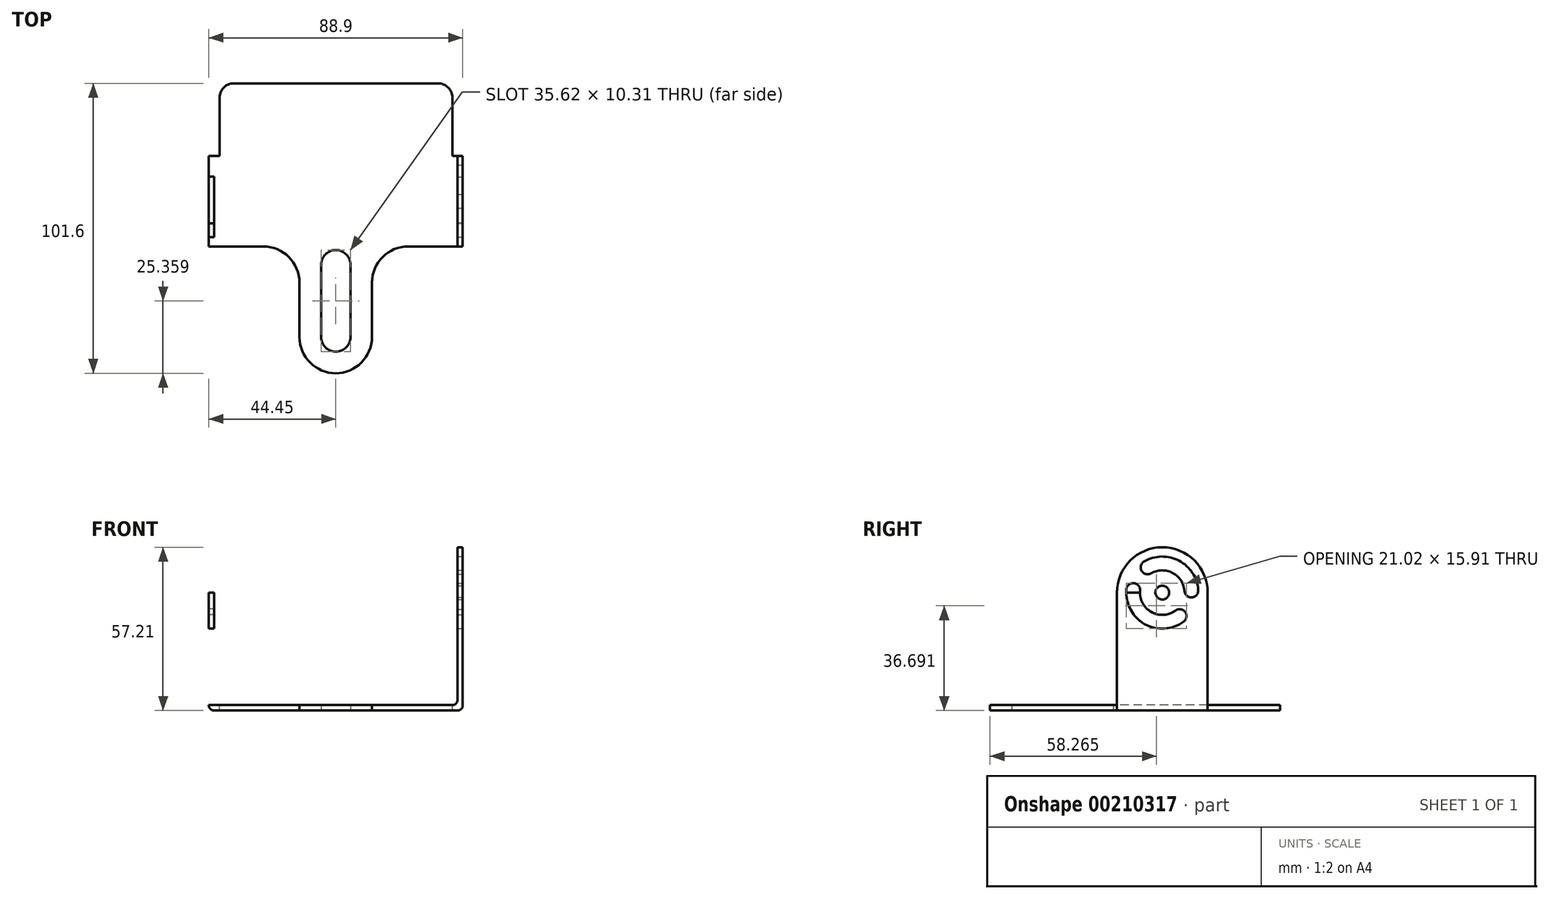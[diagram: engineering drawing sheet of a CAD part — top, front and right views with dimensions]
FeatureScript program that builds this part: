
annotation { "Feature Type Name" : "Feature", "Feature Type Description" : "" }
export const myFeature = defineFeature(function(context is Context, id is Id, definition is map)
    precondition{}
    {
        {
            var Q0;
            Q0=qCreatedBy(makeId("Top.planeOp"),FACE);
            var sketch = newSketch(context, id + "F0", { "sketchPlane" : qUnion([Q0])});
            skLineSegment(sketch, "E0.bottom", {"start": v(44.45, 15.88) * mm, "end": v(-44.45, 15.88) * mm});
            skLineSegment(sketch, "E0.top", {"start": v(44.45, -15.88) * mm, "end": v(25.4, -15.88) * mm});
            skLineSegment(sketch, "E0.left", {"start": v(44.45, 15.88) * mm, "end": v(44.45, -15.88) * mm});
            skLineSegment(sketch, "E0.right", {"start": v(-44.45, 15.88) * mm, "end": v(-44.45, -15.88) * mm});
            skPoint(sketch, "E0.middle", {"position": v(0, 0) * mm});
            skArc(sketch, "E1.0.endCap", {"start": v(12.7, -47.62) * mm, "mid": v(0, -60.33) * mm, "end": v(-12.7, -47.62) * mm});
            skLineSegment(sketch, "E1.0.left", {"start": v(12.7, -28.58) * mm, "end": v(12.7, -47.62) * mm});
            skLineSegment(sketch, "E1.0.right", {"start": v(-12.7, -28.57) * mm, "end": v(-12.7, -47.62) * mm});
            skArc(sketch, "E2.0.endCap", {"start": v(5.16, -47.62) * mm, "mid": v(0, -52.78) * mm, "end": v(-5.16, -47.62) * mm});
            skLineSegment(sketch, "E2.0.left", {"start": v(5.16, -22.32) * mm, "end": v(5.16, -47.62) * mm});
            skLineSegment(sketch, "E2.0.right", {"start": v(-5.16, -22.32) * mm, "end": v(-5.16, -47.62) * mm});
            skArc(sketch, "E3", {"start": v(5.16, -22.32) * mm, "mid": v(0, -17.16) * mm, "end": v(-5.16, -22.32) * mm});
            skLineSegment(sketch, "E4.trimOffspring", {"start": v(-25.4, -15.88) * mm, "end": v(-44.45, -15.88) * mm});
            skPoint(sketch, "E1.0.startCap.center.orphan", {"position": v(0, -15.88) * mm});
            skPoint(sketch, "E5.visualSharp", {"position": v(-12.7, -15.87) * mm});
            skArc(sketch, "E5.filletArc", {"start": v(-12.7, -28.57) * mm, "mid": v(-16.42, -19.6) * mm, "end": v(-25.4, -15.87) * mm});
            skPoint(sketch, "E6.visualSharp", {"position": v(12.7, -15.88) * mm});
            skArc(sketch, "E6.filletArc", {"start": v(25.4, -15.87) * mm, "mid": v(16.42, -19.6) * mm, "end": v(12.7, -28.57) * mm});
            skSolve(sketch);
        }
        {
            var Q0;
            Q0 = qSketchRegion(id + "F0", true);
            extrude(context, id + "F1", {"entities" : qUnion([Q0]), "depth" : 1.9 * mm, "offsetDistance" : 25.4 * mm});
        }
        {
            var Q0;
            Q0=makeQuery(id+"F1.opExtrude","SWEPT_FACE",FACE,{"disambiguationData":[OSD([sQuery(id+"F0.wireOp",EDGE,"E0.right")])]});
            var sketch = newSketch(context, id + "F2", { "sketchPlane" : qUnion([Q0])});
            skLineSegment(sketch, "E7", {"start": v(-15.87, 0) * mm, "end": v(-15.87, 41.27) * mm});
            skLineSegment(sketch, "E8", {"start": v(-15.88, 41.28) * mm, "end": v(15.88, 41.28) * mm});
            skLineSegment(sketch, "E9", {"start": v(15.87, 41.28) * mm, "end": v(15.88, 0) * mm});
            skArc(sketch, "E10", {"start": v(-15.88, 41.28) * mm, "mid": v(0, 57.15) * mm, "end": v(15.87, 41.28) * mm});
            skCircle(sketch, "E11", {"center": v(0, 41.28) * mm, "radius": 2.41 * mm});
            skArc(sketch, "E12", {"start": v(-10.1, 42.39) * mm, "mid": v(-4.48, 50.4) * mm, "end": v(5.3, 49.94) * mm});
            skArc(sketch, "E13", {"start": v(10.1, 42.39) * mm, "mid": v(5, 32.44) * mm, "end": v(-6.14, 33.18) * mm});
            skArc(sketch, "E14.0.startCap", {"start": v(-7.7, 42.12) * mm, "mid": v(-10.36, 39.99) * mm, "end": v(-12.5, 42.65) * mm});
            skArc(sketch, "E14.0.endCap", {"start": v(6.56, 52) * mm, "mid": v(7.36, 48.68) * mm, "end": v(4.04, 47.88) * mm});
            skArc(sketch, "E14.0.left", {"start": v(-12.5, 42.65) * mm, "mid": v(-5.54, 52.56) * mm, "end": v(6.56, 52) * mm});
            skArc(sketch, "E14.0.right", {"start": v(-7.7, 42.12) * mm, "mid": v(-3.41, 48.23) * mm, "end": v(4.04, 47.88) * mm});
            skArc(sketch, "E15.0.startCap", {"start": v(7.7, 42.12) * mm, "mid": v(9.84, 44.79) * mm, "end": v(12.5, 42.65) * mm});
            skArc(sketch, "E15.0.endCap", {"start": v(-7.6, 31.26) * mm, "mid": v(-8.07, 34.64) * mm, "end": v(-4.68, 35.1) * mm});
            skArc(sketch, "E15.0.left", {"start": v(12.5, 42.65) * mm, "mid": v(6.2, 30.34) * mm, "end": v(-7.6, 31.26) * mm});
            skArc(sketch, "E15.0.right", {"start": v(7.7, 42.12) * mm, "mid": v(3.82, 34.53) * mm, "end": v(-4.68, 35.1) * mm});
            skSolve(sketch);
        }
        {
            var Q0;
            {var subQ13=sQuery(id+"F2.wireOp",EDGE,"E15.0.endCap");Q0=makeQuery(id+"F2.imprint","IMPRINT",FACE,{"disambiguationData":[TD([[makeQuery(id+"F2.imprint","IMPRINT",EDGE,{"derivedFrom":subQ13}),1.0]])]});}
            var Q1;
            {var subQ1=sQuery(id+"F2.wireOp",EDGE,"E10");Q1=makeQuery(id+"F2.imprint","IMPRINT",FACE,{"disambiguationData":[TD([[makeQuery(id+"F2.imprint","IMPRINT",EDGE,{"derivedFrom":subQ1}),-1.0]])]});}
            extrude(context, id + "F3", {"entities" : qUnion([Q0, Q1]), "operationType" : NewBodyOperationType.ADD, "oppositeDirection" : true, "depth" : 1.9 * mm, "offsetDistance" : 25.4 * mm});
        }
        {
            var Q0;
            Q0=makeQuery(id+"F1.opExtrude","CAP_EDGE",EDGE,{"disambiguationData":[OSD([sQuery(id+"F0.wireOp",EDGE,"E0.right")])],"isStart":true});
            var Q1;
            Q1=makeQuery(id+"F3.opExtrude","CAP_EDGE",EDGE,{"disambiguationData":[OSD([sQuery(id+"F0.wireOp",EDGE,"E0.right")])],"isStart":false});
            fillet(context, id + "F4", {"entities" : qUnion([Q0, Q1]), "radius" : 1.84 * mm, "tangentPropagation" : true, "allowEdgeOverflow" : false});
        }
        {
            var Q0;
            Q0=makeQuery(id+"F1.opExtrude","SWEPT_FACE",FACE,{"disambiguationData":[OSD([sQuery(id+"F0.wireOp",EDGE,"E0.left")])]});
            var sketch = newSketch(context, id + "F5", { "sketchPlane" : qUnion([Q0])});
            skCircle(sketch, "E16", {"center": v(0, 41.34) * mm, "radius": 2.41 * mm});
            skArc(sketch, "E17", {"start": v(6.06, 33.12) * mm, "mid": v(-5, 32.44) * mm, "end": v(-10.17, 42.24) * mm});
            skArc(sketch, "E18", {"start": v(10.18, 42.07) * mm, "mid": v(4.77, 50.37) * mm, "end": v(-5.14, 50.16) * mm});
            skArc(sketch, "E19.0.startCap", {"start": v(4.63, 35.06) * mm, "mid": v(8, 34.55) * mm, "end": v(7.49, 31.18) * mm});
            skArc(sketch, "E19.0.endCap", {"start": v(-12.57, 42.45) * mm, "mid": v(-9.96, 44.64) * mm, "end": v(-7.77, 42.03) * mm});
            skArc(sketch, "E19.0.left", {"start": v(7.49, 31.18) * mm, "mid": v(-6.19, 30.33) * mm, "end": v(-12.57, 42.45) * mm});
            skArc(sketch, "E19.0.right", {"start": v(4.63, 35.06) * mm, "mid": v(-3.82, 34.54) * mm, "end": v(-7.77, 42.03) * mm});
            skArc(sketch, "E20.0.startCap", {"start": v(12.6, 42.24) * mm, "mid": v(10.36, 39.66) * mm, "end": v(7.78, 41.9) * mm});
            skArc(sketch, "E20.0.endCap", {"start": v(-3.93, 48.07) * mm, "mid": v(-7.23, 48.94) * mm, "end": v(-6.36, 52.24) * mm});
            skArc(sketch, "E20.0.left", {"start": v(7.78, 41.9) * mm, "mid": v(3.64, 48.23) * mm, "end": v(-3.93, 48.07) * mm});
            skArc(sketch, "E20.0.right", {"start": v(12.6, 42.24) * mm, "mid": v(5.9, 52.5) * mm, "end": v(-6.36, 52.24) * mm});
            skLineSegment(sketch, "E21", {"start": v(-15.87, 1.9) * mm, "end": v(-15.87, 41.34) * mm});
            skLineSegment(sketch, "E22", {"start": v(15.88, 1.9) * mm, "end": v(15.88, 41.34) * mm});
            skArc(sketch, "E23", {"start": v(15.88, 41.34) * mm, "mid": v(0, 57.21) * mm, "end": v(-15.88, 41.34) * mm});
            skLineSegment(sketch, "E24", {"start": v(-15.87, 1.9) * mm, "end": v(-15.87, 0) * mm});
            skLineSegment(sketch, "E25", {"start": v(-15.87, 0) * mm, "end": v(15.88, 0) * mm});
            skLineSegment(sketch, "E26", {"start": v(15.88, 0) * mm, "end": v(15.88, 1.9) * mm});
            skSolve(sketch);
        }
        {
            var Q0;
            Q0 = qSketchRegion(id + "F5", true);
            extrude(context, id + "F6", {"entities" : qUnion([Q0]), "operationType" : NewBodyOperationType.ADD, "oppositeDirection" : true, "depth" : 1.84 * mm, "offsetDistance" : 25.4 * mm});
        }
        {
            var Q0;
            Q0=makeQuery(id+"F1.opExtrude","CAP_EDGE",EDGE,{"disambiguationData":[OSD([sQuery(id+"F0.wireOp",EDGE,"E0.left")])],"isStart":true});
            var Q1;
            Q1=makeQuery(id+"F6.boolean.opBoolean","INTERSECT",EDGE,{"derivedFrom":[makeQuery(id+"F1.opExtrude","CAP_FACE",FACE,{"disambiguationData":[OSD([sQuery(id+"F0.wireOp",EDGE,"E0.bottom"),sQuery(id+"F0.wireOp",EDGE,"E0.top"),sQuery(id+"F0.wireOp",EDGE,"E0.left"),sQuery(id+"F0.wireOp",EDGE,"E0.right"),sQuery(id+"F0.wireOp",EDGE,"E1.0.endCap"),sQuery(id+"F0.wireOp",EDGE,"E1.0.left"),sQuery(id+"F0.wireOp",EDGE,"E1.0.right"),sQuery(id+"F0.wireOp",EDGE,"E2.0.endCap"),sQuery(id+"F0.wireOp",EDGE,"E2.0.left"),sQuery(id+"F0.wireOp",EDGE,"E2.0.right"),sQuery(id+"F0.wireOp",EDGE,"E3"),sQuery(id+"F0.wireOp",EDGE,"E4.trimOffspring"),sQuery(id+"F0.wireOp",EDGE,"E5.filletArc"),sQuery(id+"F0.wireOp",EDGE,"E6.filletArc")])],"isStart":false}),makeQuery(id+"F6.opExtrude","CAP_FACE",FACE,{"disambiguationData":[OSD([sQuery(id+"F5.wireOp",EDGE,"E16"),sQuery(id+"F5.wireOp",EDGE,"E19.0.startCap"),sQuery(id+"F5.wireOp",EDGE,"E19.0.endCap"),sQuery(id+"F5.wireOp",EDGE,"E19.0.left"),sQuery(id+"F5.wireOp",EDGE,"E19.0.right"),sQuery(id+"F5.wireOp",EDGE,"E20.0.startCap"),sQuery(id+"F5.wireOp",EDGE,"E20.0.endCap"),sQuery(id+"F5.wireOp",EDGE,"E20.0.left"),sQuery(id+"F5.wireOp",EDGE,"E20.0.right"),sQuery(id+"F5.wireOp",EDGE,"E21"),sQuery(id+"F5.wireOp",EDGE,"E22"),sQuery(id+"F5.wireOp",EDGE,"E23"),sQuery(id+"F5.wireOp",EDGE,"E24"),sQuery(id+"F5.wireOp",EDGE,"E25"),sQuery(id+"F5.wireOp",EDGE,"E26")])],"isStart":false})]});
            fillet(context, id + "F7", {"entities" : qUnion([Q0, Q1]), "radius" : 1.78 * mm, "tangentPropagation" : true, "allowEdgeOverflow" : false});
        }
        {
            var Q0;
            Q0=makeQuery(id+"F6.boolean.opBoolean","MERGE",FACE,{"derivedFrom":[makeQuery(id+"F3.boolean.opBoolean","MERGE",FACE,{"derivedFrom":[makeQuery(id+"F1.opExtrude","SWEPT_FACE",FACE,{"disambiguationData":[OSD([sQuery(id+"F0.wireOp",EDGE,"E0.bottom")])]}),makeQuery(id+"F3.opExtrude","SWEPT_FACE",FACE,{"disambiguationData":[OSD([sQuery(id+"F2.wireOp",EDGE,"E7")])]})]}),makeQuery(id+"F6.opExtrude","SWEPT_FACE",FACE,{"disambiguationData":[OSD([sQuery(id+"F5.wireOp",EDGE,"E22"),sQuery(id+"F5.wireOp",EDGE,"E26")])]})]});
            var sketch = newSketch(context, id + "F8", { "sketchPlane" : qUnion([Q0])});
            skLineSegment(sketch, "E27.bottom", {"start": v(-40.83, 0) * mm, "end": v(40.7, 0) * mm});
            skLineSegment(sketch, "E27.top", {"start": v(-40.83, 1.9) * mm, "end": v(40.7, 1.9) * mm});
            skLineSegment(sketch, "E27.left", {"start": v(-40.83, 0) * mm, "end": v(-40.83, 1.9) * mm});
            skLineSegment(sketch, "E27.right", {"start": v(40.7, 0) * mm, "end": v(40.7, 1.9) * mm});
            skSolve(sketch);
        }
        {
            var Q0;
            Q0 = qSketchRegion(id + "F8", true);
            extrude(context, id + "F9", {"entities" : qUnion([Q0]), "operationType" : NewBodyOperationType.ADD, "depth" : 25.4 * mm, "offsetDistance" : 25.4 * mm});
        }
        {
            var Q0;
            Q0=makeQuery(id+"F9.opExtrude","CAP_EDGE",EDGE,{"disambiguationData":[OSD([sQuery(id+"F8.wireOp",EDGE,"E27.left")])],"isStart":false});
            var Q1;
            Q1=makeQuery(id+"F9.opExtrude","CAP_EDGE",EDGE,{"disambiguationData":[OSD([sQuery(id+"F8.wireOp",EDGE,"E27.right")])],"isStart":false});
            fillet(context, id + "F10", {"entities" : qUnion([Q0, Q1]), "radius" : 5.08 * mm, "tangentPropagation" : true, "allowEdgeOverflow" : false});
        }
    });
